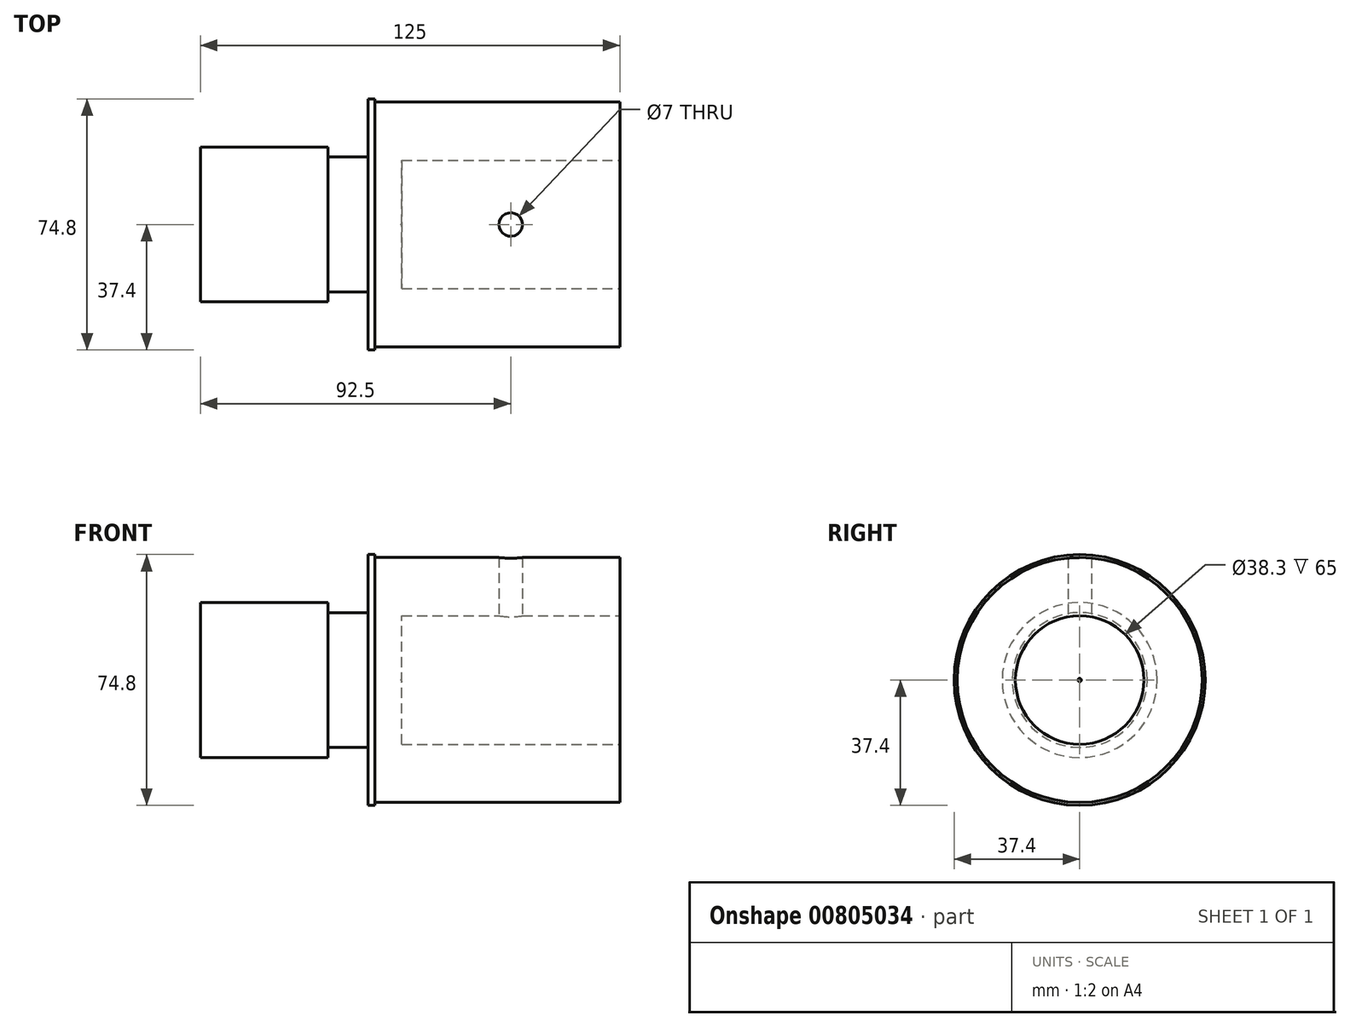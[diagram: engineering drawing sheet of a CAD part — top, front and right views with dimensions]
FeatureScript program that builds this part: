
annotation { "Feature Type Name" : "Feature", "Feature Type Description" : "" }
export const myFeature = defineFeature(function(context is Context, id is Id, definition is map)
    precondition{}
    {
        {
            var Q0;
            Q0=qCreatedBy(makeId("Front.planeOp"),FACE);
            var sketch = newSketch(context, id + "F0", { "sketchPlane" : qUnion([Q0])});
            skLineSegment(sketch, "E0", {"start": v(0, 0) * mm, "end": v(0, 23.1) * mm});
            skLineSegment(sketch, "E1", {"start": v(0, 23.1) * mm, "end": v(38, 23.1) * mm});
            skLineSegment(sketch, "E2", {"start": v(38, 23.1) * mm, "end": v(38, 20.1) * mm});
            skLineSegment(sketch, "E3", {"start": v(38, 20.1) * mm, "end": v(50, 20.1) * mm});
            skLineSegment(sketch, "E4", {"start": v(50, 20.1) * mm, "end": v(50, 36.5) * mm});
            skLineSegment(sketch, "E5", {"start": v(52, 36.5) * mm, "end": v(125, 36.5) * mm});
            skLineSegment(sketch, "E6", {"start": v(125, 36.5) * mm, "end": v(125, 0) * mm});
            skLineSegment(sketch, "E7", {"start": v(125, 0) * mm, "end": v(0, 0) * mm});
            skLineSegment(sketch, "E8", {"start": v(50, 36.5) * mm, "end": v(50, 37.4) * mm});
            skLineSegment(sketch, "E9", {"start": v(50, 37.4) * mm, "end": v(52, 37.4) * mm});
            skLineSegment(sketch, "E10", {"start": v(52, 37.4) * mm, "end": v(52, 36.5) * mm});
            skSolve(sketch);
        }
        {
            var Q0;
            Q0=makeQuery(id+"F0.imprint","IMPRINT",FACE,{"disambiguationData":[TD([[makeQuery(id+"F0.imprint","IMPRINT",EDGE,{"derivedFrom":sQuery(id+"F0.wireOp",EDGE,"E0")}),-1.0]])]});
            var Q1;
            {var subQ3=sQuery(id+"F0.wireOp",EDGE,"oPnuAlFy-IrYi-2yoG-jHFL-xciEVcSRY0PP");Q1=makeQuery(id+"F0.imprint","IMPRINT",FACE,{"disambiguationData":[TD([[makeQuery(id+"F0.imprint","IMPRINT",EDGE,{"derivedFrom":subQ3}),1.0]])]});}
            var Q2;
            {var subQ0=sQuery(id+"F0.wireOp",EDGE,"E8");Q2=makeQuery(id+"F0.imprint","IMPRINT",FACE,{"disambiguationData":[TD([[makeQuery(id+"F0.imprint","IMPRINT",EDGE,{"derivedFrom":subQ0}),-1.0]])]});}
            var Q3;
            Q3=sQuery(id+"F0.wireOp",EDGE,"E7");
            revolve(context, id + "F1", {"surfaceOperationType" : NewSurfaceOperationType.NEW, "entities" : qUnion([Q0, Q1, Q2]), "axis" : qUnion([Q3]), "revolveType" : RevolveType.FULL});
        }
        {
            var Q0;
            Q0=makeQuery(id+"F1.opRevolve","SWEPT_FACE",FACE,{"disambiguationData":[OSD([sQuery(id+"F0.wireOp",EDGE,"E6")])]});
            var sketch = newSketch(context, id + "F2", { "sketchPlane" : qUnion([Q0])});
            skPoint(sketch, "E11", {"position": v(0, 0) * mm});
            skSolve(sketch);
        }
        {
            var Q0;
            Q0=sQuery(id+"F2.wireOp",VERTEX,"E11");
            var Q1;
            Q1=makeQuery(id+"F1.opRevolve","SWEPT_BODY",BODY,{"disambiguationData":[OSD([sQuery(id+"F0.wireOp",EDGE,"E0"),sQuery(id+"F0.wireOp",EDGE,"E1"),sQuery(id+"F0.wireOp",EDGE,"E2"),sQuery(id+"F0.wireOp",EDGE,"E3"),sQuery(id+"F0.wireOp",EDGE,"E4"),sQuery(id+"F0.wireOp",EDGE,"E5"),sQuery(id+"F0.wireOp",EDGE,"E6"),sQuery(id+"F0.wireOp",EDGE,"E7"),sQuery(id+"F0.wireOp",EDGE,"E8"),sQuery(id+"F0.wireOp",EDGE,"E9"),sQuery(id+"F0.wireOp",EDGE,"E10")])]});
            hole(context, id + "F3", {"style" : HoleStyle.C_BORE, "endStyle" : HoleEndStyle.BLIND, "holeDiameter" : 1 * mm, "cBoreDiameter" : 38.3 * mm, "cBoreDepth" : 65 * mm, "majorDiameter" : 5 * mm, "holeDepth" : 65 * mm, "isTappedThrough" : true, "tappedDepth" : 22 * mm, "tapClearance" : 3, "startFromSketch" : true, "locations" : qUnion([Q0]), "scope" : qUnion([Q1])});
        }
        {
            var Q0;
            Q0=qCreatedBy(makeId("Top.planeOp"),FACE);
            var sketch = newSketch(context, id + "F4", { "sketchPlane" : qUnion([Q0])});
            skPoint(sketch, "E12", {"position": v(92.5, 0) * mm});
            skSolve(sketch);
        }
        {
            var Q0;
            Q0=sQuery(id+"F4.wireOp",VERTEX,"E12");
            var Q1;
            Q1=makeQuery(id+"F1.opRevolve","SWEPT_BODY",BODY,{"disambiguationData":[OSD([sQuery(id+"F0.wireOp",EDGE,"E0"),sQuery(id+"F0.wireOp",EDGE,"E1"),sQuery(id+"F0.wireOp",EDGE,"E2"),sQuery(id+"F0.wireOp",EDGE,"E3"),sQuery(id+"F0.wireOp",EDGE,"E4"),sQuery(id+"F0.wireOp",EDGE,"E5"),sQuery(id+"F0.wireOp",EDGE,"E6"),sQuery(id+"F0.wireOp",EDGE,"E7"),sQuery(id+"F0.wireOp",EDGE,"E8"),sQuery(id+"F0.wireOp",EDGE,"E9"),sQuery(id+"F0.wireOp",EDGE,"E10")])]});
            hole(context, id + "F5", {"style" : HoleStyle.SIMPLE, "endStyle" : HoleEndStyle.THROUGH, "oppositeDirection" : true, "standardTappedOrClearance" : lookupTablePath({ "standard" : "ISO", "engagement" : "75%", "pitch" : "1 mm", "size" : "M8", "type" : "Tapped" }), "standardBlindInLast" : lookupTablePath({ "standard" : "ISO", "engagement" : "75%", "pitch" : "1 mm", "size" : "M8", "type" : "Tapped" }), "holeDiameter" : 7 * mm, "majorDiameter" : 8 * mm, "showTappedDepth" : true, "isTappedThrough" : true, "tappedDepth" : 22 * mm, "tapClearance" : 3, "startFromSketch" : true, "locations" : qUnion([Q0]), "scope" : qUnion([Q1])});
        }
    });
